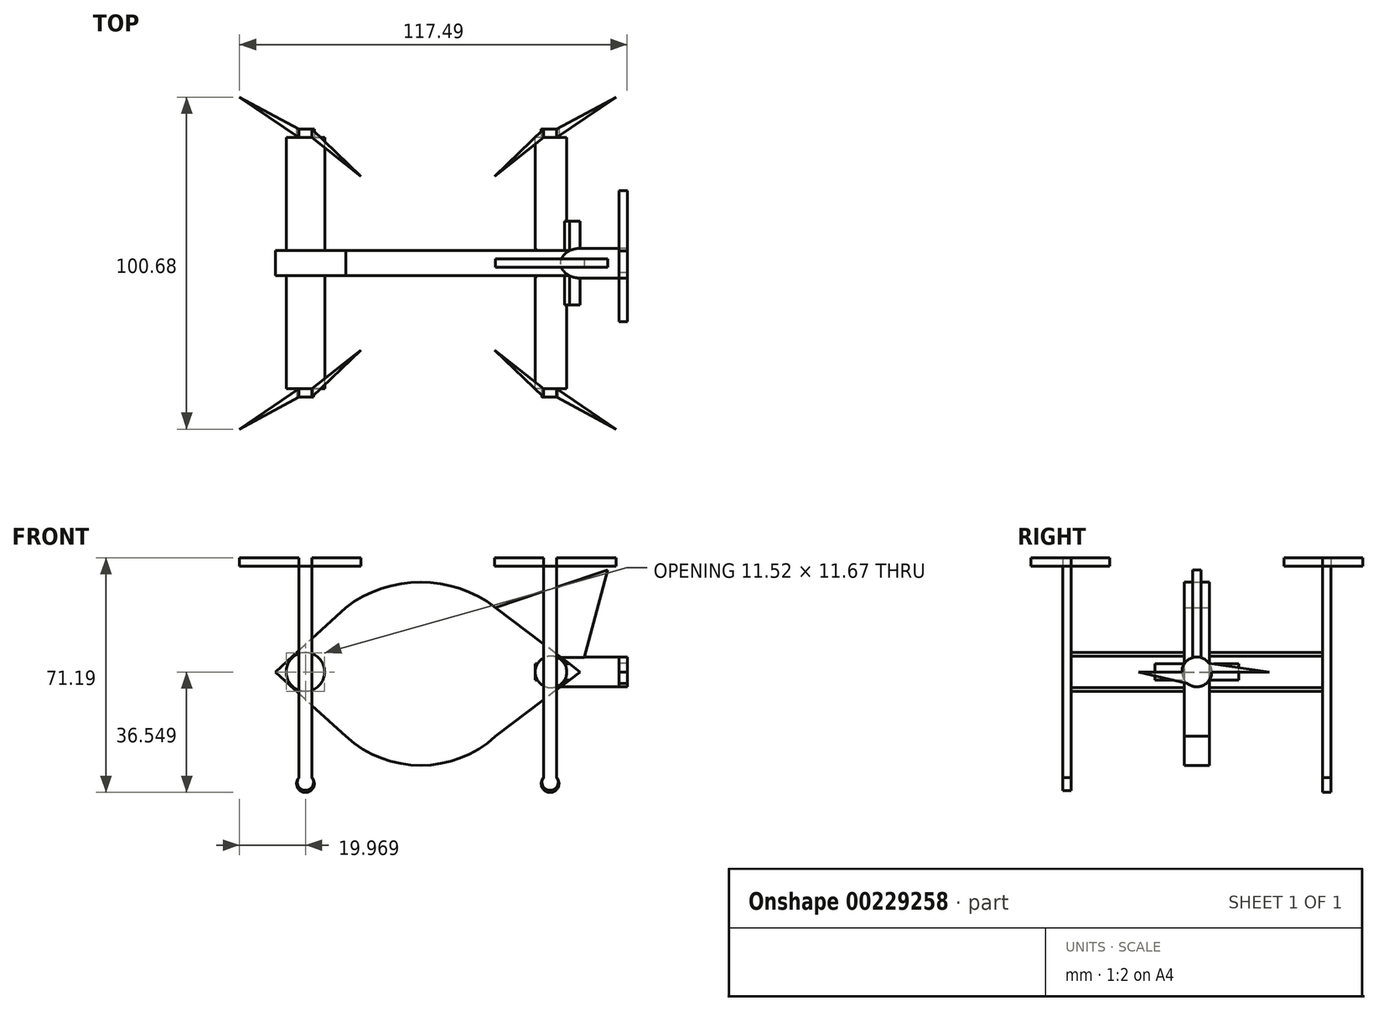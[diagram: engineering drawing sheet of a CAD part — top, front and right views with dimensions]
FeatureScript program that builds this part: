
annotation { "Feature Type Name" : "Feature", "Feature Type Description" : "" }
export const myFeature = defineFeature(function(context is Context, id is Id, definition is map)
    precondition{}
    {
        {
            var Q0;
            Q0=qCreatedBy(makeId("Front.planeOp"),FACE);
            var sketch = newSketch(context, id + "F0", { "sketchPlane" : qUnion([Q0])});
            skPoint(sketch, "E0.middle", {"position": v(0, 0) * mm});
            skLineSegment(sketch, "E1", {"start": v(46.2, 0) * mm, "end": v(20.54, 19.54) * mm});
            skLineSegment(sketch, "E2", {"start": v(46.2, 0) * mm, "end": v(20.54, -19.54) * mm});
            skLineSegment(sketch, "E3", {"start": v(-46.2, 0) * mm, "end": v(-24.82, 19.54) * mm});
            skLineSegment(sketch, "E4", {"start": v(-46.2, 0) * mm, "end": v(-24.82, -19.54) * mm});
            skArc(sketch, "E5", {"start": v(20.54, 19.54) * mm, "mid": v(-2.14, 27.19) * mm, "end": v(-24.82, 19.54) * mm});
            skArc(sketch, "E6", {"start": v(-24.82, -19.54) * mm, "mid": v(-2.14, -28.34) * mm, "end": v(20.54, -19.54) * mm});
            skCircle(sketch, "E7", {"center": v(-37.08, 0) * mm, "radius": 5.85 * mm});
            skCircle(sketch, "E8", {"center": v(37.37, 0) * mm, "radius": 4.78 * mm});
            skLineSegment(sketch, "E9", {"start": v(20.54, 19.54) * mm, "end": v(54.48, 30.95) * mm});
            skLineSegment(sketch, "E10", {"start": v(54.48, 30.95) * mm, "end": v(46.2, 0) * mm});
            skLineSegment(sketch, "E11.bottom", {"start": v(57.9, 2.42) * mm, "end": v(34.51, 2.42) * mm});
            skLineSegment(sketch, "E11.top", {"start": v(57.9, -2.42) * mm, "end": v(34.51, -2.42) * mm});
            skLineSegment(sketch, "E11.left", {"start": v(57.9, 2.42) * mm, "end": v(57.9, -2.42) * mm});
            skLineSegment(sketch, "E11.right", {"start": v(34.51, 2.42) * mm, "end": v(34.51, -2.42) * mm});
            skPoint(sketch, "E11.middle", {"position": v(46.2, 0) * mm});
            skSolve(sketch);
        }
        {
            var Q0;
            {var subQ1=sQuery(id+"F0.wireOp",EDGE,"E1");Q0=makeQuery(id+"F0.imprint","IMPRINT",FACE,{"disambiguationData":[TD([[makeQuery(id+"F0.imprint","IMPRINT",EDGE,{"derivedFrom":subQ1}),1.0]])]});}
            var Q1;
            {var subQ1=sQuery(id+"F0.wireOp",EDGE,"E2");Q1=makeQuery(id+"F0.imprint","IMPRINT",FACE,{"disambiguationData":[TD([[makeQuery(id+"F0.imprint","IMPRINT",EDGE,{"derivedFrom":subQ1}),-1.0]])]});}
            extrude(context, id + "F1", {"entities" : qUnion([Q0, Q1]), "endBound" : BoundingType.SYMMETRIC, "depth" : 25.4 * mm});
        }
        {
            var Q0;
            Q0=makeQuery(id+"F0.imprint","IMPRINT",FACE,{"disambiguationData":[TD([[makeQuery(id+"F0.imprint","IMPRINT",EDGE,{"derivedFrom":sQuery(id+"F0.wireOp",EDGE,"E7")}),1.0]])]});
            var Q1;
            Q1=makeQuery(id+"F0.imprint","IMPRINT",FACE,{"disambiguationData":[TD([[makeQuery(id+"F0.imprint","IMPRINT",EDGE,{"derivedFrom":sQuery(id+"F0.wireOp",EDGE,"E8")}),1.0]])]});
            extrude(context, id + "F2", {"entities" : qUnion([Q0, Q1]), "operationType" : NewBodyOperationType.ADD, "endBound" : BoundingType.SYMMETRIC, "depth" : 76.2 * mm});
        }
        {
            var Q0;
            Q0=makeQuery(id+"F2.opExtrude","CAP_FACE",FACE,{"disambiguationData":[OSD([sQuery(id+"F0.wireOp",EDGE,"E7")])],"isStart":false});
            var sketch = newSketch(context, id + "F3", { "sketchPlane" : qUnion([Q0])});
            skLineSegment(sketch, "E12.bottom", {"start": v(-39.08, 32.09) * mm, "end": v(-35.08, 32.09) * mm});
            skLineSegment(sketch, "E12.top", {"start": v(-39.08, -32.09) * mm, "end": v(-35.08, -32.09) * mm});
            skLineSegment(sketch, "E12.left", {"start": v(-39.08, 32.09) * mm, "end": v(-39.08, -32.09) * mm});
            skLineSegment(sketch, "E12.right", {"start": v(-35.08, 32.09) * mm, "end": v(-35.08, -32.09) * mm});
            skPoint(sketch, "E12.middle", {"position": v(-37.08, 0) * mm});
            skArc(sketch, "E13", {"start": v(-39.08, -32.09) * mm, "mid": v(-37.08, -35.94) * mm, "end": v(-35.08, -32.09) * mm});
            skLineSegment(sketch, "E14.MirrorCS", {"start": v(39.08, 32.09) * mm, "end": v(39.08, -32.09) * mm});
            skLineSegment(sketch, "E15.MirrorCS", {"start": v(35.08, 32.09) * mm, "end": v(35.08, -32.09) * mm});
            skArc(sketch, "E16.MirrorCS", {"start": v(39.08, -32.09) * mm, "mid": v(37.08, -35.94) * mm, "end": v(35.08, -32.09) * mm});
            skLineSegment(sketch, "E17.MirrorCS", {"start": v(39.08, 32.09) * mm, "end": v(35.08, 32.09) * mm});
            skSolve(sketch);
        }
        {
            var Q0;
            Q0 = qSketchRegion(id + "F3", true);
            extrude(context, id + "F4", {"entities" : qUnion([Q0]), "operationType" : NewBodyOperationType.ADD, "depth" : 2.54 * mm});
        }
        {
            var Q0;
            Q0=makeQuery(id+"F2.opExtrude","CAP_FACE",FACE,{"disambiguationData":[OSD([sQuery(id+"F0.wireOp",EDGE,"E7")])],"isStart":true});
            var sketch = newSketch(context, id + "F5", { "sketchPlane" : qUnion([Q0])});
            skLineSegment(sketch, "E18.bottom", {"start": v(39.08, 32.09) * mm, "end": v(35.08, 32.09) * mm});
            skLineSegment(sketch, "E18.top", {"start": v(39.08, -32.09) * mm, "end": v(35.08, -32.09) * mm});
            skLineSegment(sketch, "E18.left", {"start": v(39.08, 32.09) * mm, "end": v(39.08, -32.09) * mm});
            skLineSegment(sketch, "E18.right", {"start": v(35.08, 32.09) * mm, "end": v(35.08, -32.09) * mm});
            skPoint(sketch, "E18.middle", {"position": v(37.08, 0) * mm});
            skArc(sketch, "E19", {"start": v(35.08, -32.09) * mm, "mid": v(37.08, -36.56) * mm, "end": v(39.08, -32.09) * mm});
            skLineSegment(sketch, "E20.MirrorCS", {"start": v(-35.08, 32.09) * mm, "end": v(-35.08, -32.09) * mm});
            skLineSegment(sketch, "E21.MirrorCS", {"start": v(-39.08, 32.09) * mm, "end": v(-39.08, -32.09) * mm});
            skLineSegment(sketch, "E22.MirrorCS", {"start": v(-39.08, 32.09) * mm, "end": v(-35.08, 32.09) * mm});
            skArc(sketch, "E23.MirrorCS", {"start": v(-35.08, -32.09) * mm, "mid": v(-37.08, -36.56) * mm, "end": v(-39.08, -32.09) * mm});
            skSolve(sketch);
        }
        {
            var Q0;
            Q0 = qSketchRegion(id + "F5", true);
            extrude(context, id + "F6", {"entities" : qUnion([Q0]), "operationType" : NewBodyOperationType.ADD, "depth" : 2.54 * mm});
        }
        {
            var Q0;
            Q0=makeQuery(id+"F6.opExtrude","SWEPT_FACE",FACE,{"disambiguationData":[OSD([sQuery(id+"F5.wireOp",EDGE,"E18.bottom")])]});
            var sketch = newSketch(context, id + "F7", { "sketchPlane" : qUnion([Q0])});
            skLineSegment(sketch, "E24", {"start": v(-39.08, 40.64) * mm, "end": v(-57.05, 50.34) * mm});
            skLineSegment(sketch, "E25", {"start": v(-57.05, 50.34) * mm, "end": v(-39.08, 38.1) * mm});
            skLineSegment(sketch, "E26", {"start": v(-35.08, 38.1) * mm, "end": v(-20.25, 26.38) * mm});
            skLineSegment(sketch, "E27", {"start": v(-20.25, 26.38) * mm, "end": v(-35.08, 40.64) * mm});
            skLineSegment(sketch, "E28.MirrorCS", {"start": v(20.25, 26.38) * mm, "end": v(35.08, 40.64) * mm});
            skLineSegment(sketch, "E29.MirrorCS", {"start": v(35.08, 38.1) * mm, "end": v(20.25, 26.38) * mm});
            skLineSegment(sketch, "E30.MirrorCS", {"start": v(39.08, 40.64) * mm, "end": v(57.05, 50.34) * mm});
            skLineSegment(sketch, "E31.MirrorCS", {"start": v(57.05, 50.34) * mm, "end": v(39.08, 38.1) * mm});
            skLineSegment(sketch, "E32.MirrorCS", {"start": v(-39.08, -40.64) * mm, "end": v(-57.05, -50.34) * mm});
            skLineSegment(sketch, "E33.MirrorCS", {"start": v(-57.05, -50.34) * mm, "end": v(-39.08, -38.1) * mm});
            skLineSegment(sketch, "E34.MirrorCS", {"start": v(-20.25, -26.38) * mm, "end": v(-35.08, -40.64) * mm});
            skLineSegment(sketch, "E35.MirrorCS", {"start": v(-35.08, -38.1) * mm, "end": v(-20.25, -26.38) * mm});
            skLineSegment(sketch, "E36.MirrorCS", {"start": v(20.25, -26.38) * mm, "end": v(35.08, -40.64) * mm});
            skLineSegment(sketch, "E37.MirrorCS", {"start": v(35.08, -38.1) * mm, "end": v(20.25, -26.38) * mm});
            skLineSegment(sketch, "E38.MirrorCS", {"start": v(39.08, -40.64) * mm, "end": v(57.05, -50.34) * mm});
            skLineSegment(sketch, "E39.MirrorCS", {"start": v(57.05, -50.34) * mm, "end": v(39.08, -38.1) * mm});
            skLineSegment(sketch, "E40", {"start": v(-39.08, 40.64) * mm, "end": v(-39.08, 38.1) * mm});
            skLineSegment(sketch, "E41", {"start": v(-35.08, 40.64) * mm, "end": v(-35.08, 38.1) * mm});
            skLineSegment(sketch, "E42", {"start": v(35.08, 38.1) * mm, "end": v(35.08, 40.64) * mm});
            skLineSegment(sketch, "E43", {"start": v(39.08, 40.64) * mm, "end": v(39.08, 38.1) * mm});
            skLineSegment(sketch, "E44", {"start": v(-39.08, -38.1) * mm, "end": v(-39.08, -40.64) * mm});
            skLineSegment(sketch, "E45", {"start": v(-35.08, -38.1) * mm, "end": v(-35.08, -40.64) * mm});
            skLineSegment(sketch, "E46", {"start": v(35.08, -38.1) * mm, "end": v(35.08, -40.64) * mm});
            skLineSegment(sketch, "E47", {"start": v(39.08, -38.1) * mm, "end": v(39.08, -40.64) * mm});
            skSolve(sketch);
        }
        {
            var Q0;
            Q0 = qSketchRegion(id + "F7", true);
            extrude(context, id + "F8", {"entities" : qUnion([Q0]), "depth" : 2.54 * mm});
        }
        {
            var Q0;
            {var subQ0=sQuery(id+"F0.wireOp",EDGE,"E11.left");Q0=makeQuery(id+"F0.imprint","IMPRINT",FACE,{"disambiguationData":[TD([[makeQuery(id+"F0.imprint","IMPRINT",EDGE,{"derivedFrom":subQ0}),-1.0]])]});}
            var Q1;
            {var subQ0=sQuery(id+"F0.wireOp",EDGE,"E10");var subQ3=sQuery(id+"F0.wireOp",EDGE,"E11.bottom");var subQ5=makeQuery(id+"F0.imprint","INTERSECT",VERTEX,{"derivedFrom":[subQ0,subQ3]});Q1=makeQuery(id+"F0.imprint","IMPRINT",FACE,{"disambiguationData":[TD([[makeQuery(id+"F0.imprint","IMPRINT",EDGE,{"disambiguationData":[TD([[subQ5,-1.0]])],"derivedFrom":subQ3}),1.0]])]});}
            var Q2;
            {var subQ0=sQuery(id+"F0.wireOp",EDGE,"E11.bottom");var subQ1=sQuery(id+"F0.wireOp",EDGE,"E8");var subQ2=makeQuery(id+"F0.imprint","INTERSECT",VERTEX,{"derivedFrom":[subQ1,subQ0]});Q2=makeQuery(id+"F0.imprint","IMPRINT",FACE,{"disambiguationData":[TD([[makeQuery(id+"F0.imprint","IMPRINT",EDGE,{"disambiguationData":[TD([[subQ2,1.0]])],"derivedFrom":subQ1}),-1.0]])]});}
            var Q3;
            Q3=makeQuery(id+"F0.imprint","IMPRINT",FACE,{"disambiguationData":[TD([[makeQuery(id+"F0.imprint","IMPRINT",EDGE,{"derivedFrom":sQuery(id+"F0.wireOp",EDGE,"E3")}),-1.0]])]});
            extrude(context, id + "F9", {"entities" : qUnion([Q0, Q1, Q2, Q3]), "operationType" : NewBodyOperationType.ADD, "endBound" : BoundingType.SYMMETRIC, "depth" : 7.62 * mm});
        }
        {
            var Q0;
            Q0=makeQuery(id+"F9.opExtrude","SWEPT_FACE",FACE,{"disambiguationData":[OSD([sQuery(id+"F0.wireOp",EDGE,"E11.left")])]});
            var sketch = newSketch(context, id + "F10", { "sketchPlane" : qUnion([Q0])});
            skCircle(sketch, "E48", {"center": v(0, 0) * mm, "radius": 4.52 * mm});
            skSolve(sketch);
        }
        {
            var Q0;
            Q0 = qSketchRegion(id + "F10", true);
            extrude(context, id + "F11", {"entities" : qUnion([Q0]), "operationType" : NewBodyOperationType.ADD, "oppositeDirection" : true, "depth" : 25.4 * mm});
        }
        {
            var Q0;
            Q0=makeQuery(id+"F11.boolean.opBoolean","MERGE",FACE,{"derivedFrom":[makeQuery(id+"F9.opExtrude","SWEPT_FACE",FACE,{"disambiguationData":[OSD([sQuery(id+"F0.wireOp",EDGE,"E11.left")])]}),makeQuery(id+"F11.opExtrude","CAP_FACE",FACE,{"disambiguationData":[OSD([sQuery(id+"F10.wireOp",EDGE,"E48")])],"isStart":true})]});
            var sketch = newSketch(context, id + "F12", { "sketchPlane" : qUnion([Q0])});
            skLineSegment(sketch, "E49", {"start": v(0, 4.52) * mm, "end": v(0, 19.54) * mm});
            skLineSegment(sketch, "E50", {"start": v(0, 19.54) * mm, "end": v(-3.57, 4.52) * mm});
            skLineSegment(sketch, "E51", {"start": v(-4.52, 0) * mm, "end": v(-17.68, 0) * mm});
            skLineSegment(sketch, "E52", {"start": v(-17.68, 0) * mm, "end": v(-2.9, -3.46) * mm});
            skLineSegment(sketch, "E53", {"start": v(0, -4.52) * mm, "end": v(0, -16.97) * mm});
            skLineSegment(sketch, "E54", {"start": v(3.73, 0) * mm, "end": v(21.96, 0) * mm});
            skLineSegment(sketch, "E55", {"start": v(21.96, 0) * mm, "end": v(3.68, 2.62) * mm});
            skCircle(sketch, "E56", {"center": v(0, 0) * mm, "radius": 4.52 * mm});
            skPoint(sketch, "E57.end.orphan", {"position": v(3.73, -3.46) * mm});
            skLineSegment(sketch, "E58", {"start": v(0, -16.97) * mm, "end": v(1.78, -4.52) * mm});
            skSolve(sketch);
        }
        {
            var Q0;
            Q0 = qSketchRegion(id + "F12", true);
            extrude(context, id + "F13", {"entities" : qUnion([Q0]), "depth" : 2.54 * mm});
        }
        {
            var Q0;
            {var subQ0=sQuery(id+"F0.wireOp",EDGE,"E9");Q0=makeQuery(id+"F0.imprint","IMPRINT",FACE,{"disambiguationData":[TD([[makeQuery(id+"F0.imprint","IMPRINT",EDGE,{"derivedFrom":subQ0}),-1.0]])]});}
            extrude(context, id + "F14", {"entities" : qUnion([Q0]), "operationType" : NewBodyOperationType.ADD, "endBound" : BoundingType.SYMMETRIC, "depth" : 2.54 * mm});
        }
    });
